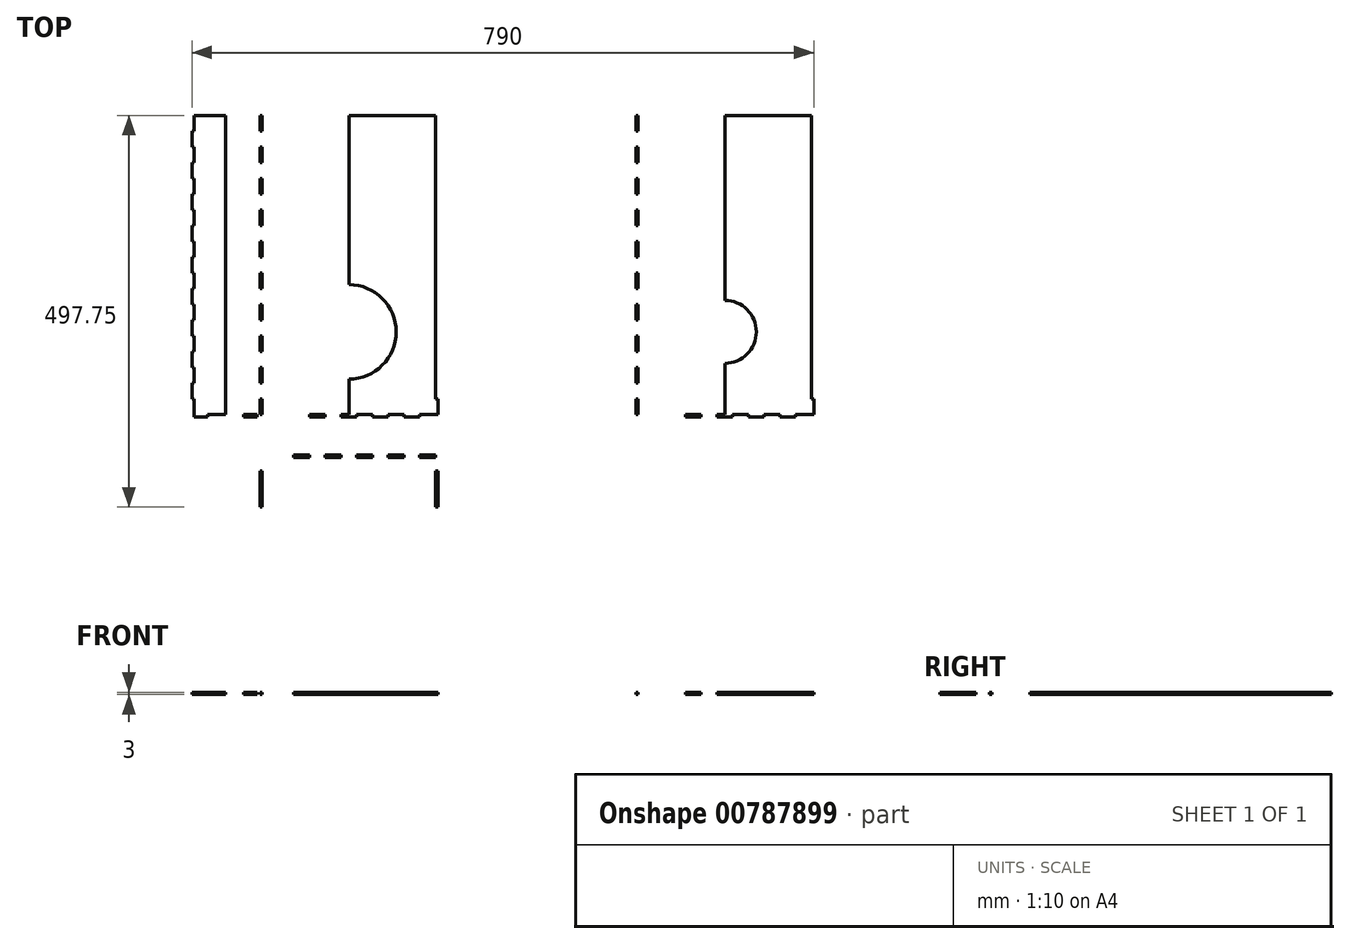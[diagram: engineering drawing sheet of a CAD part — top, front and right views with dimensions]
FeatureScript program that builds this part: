
annotation { "Feature Type Name" : "Feature", "Feature Type Description" : "" }
export const myFeature = defineFeature(function(context is Context, id is Id, definition is map)
    precondition{}
    {
        {
            var Q0;
            Q0=qCreatedBy(makeId("Top.planeOp"),FACE);
            var sketch = newSketch(context, id + "F0", { "sketchPlane" : qUnion([Q0])});
            skCircle(sketch, "E0", {"center": v(0, 0) * mm, "radius": 60 * mm});
            skLineSegment(sketch, "E1.bottom", {"start": v(0, -105) * mm, "end": v(110, -105) * mm});
            skLineSegment(sketch, "E1.top", {"start": v(0, 275) * mm, "end": v(110, 275) * mm});
            skLineSegment(sketch, "E1.left", {"start": v(0, -105) * mm, "end": v(0, 275) * mm});
            skLineSegment(sketch, "E1.right", {"start": v(110, -105) * mm, "end": v(110, 275) * mm});
            skLineSegment(sketch, "E2.bottom", {"start": v(110, -105) * mm, "end": v(113, -105) * mm});
            skLineSegment(sketch, "E2.top", {"start": v(110, -85) * mm, "end": v(113, -85) * mm});
            skLineSegment(sketch, "E2.left", {"start": v(110, -105) * mm, "end": v(110, -85) * mm});
            skLineSegment(sketch, "E2.right", {"start": v(113, -105) * mm, "end": v(113, -85) * mm});
            skLineSegment(sketch, "E3.0.1.0", {"start": v(110, -65) * mm, "end": v(110, -45) * mm});
            skLineSegment(sketch, "E3.0.1.1", {"start": v(113, -65) * mm, "end": v(113, -45) * mm});
            skLineSegment(sketch, "E3.0.1.2", {"start": v(110, -45) * mm, "end": v(113, -45) * mm});
            skLineSegment(sketch, "E3.0.1.3", {"start": v(110, -65) * mm, "end": v(113, -65) * mm});
            skLineSegment(sketch, "E3.0.2.0", {"start": v(110, -25) * mm, "end": v(110, -5) * mm});
            skLineSegment(sketch, "E3.0.2.1", {"start": v(113, -25) * mm, "end": v(113, -5) * mm});
            skLineSegment(sketch, "E3.0.2.2", {"start": v(110, -5) * mm, "end": v(113, -5) * mm});
            skLineSegment(sketch, "E3.0.2.3", {"start": v(110, -25) * mm, "end": v(113, -25) * mm});
            skLineSegment(sketch, "E3.0.3.0", {"start": v(110, 15) * mm, "end": v(110, 35) * mm});
            skLineSegment(sketch, "E3.0.3.1", {"start": v(113, 15) * mm, "end": v(113, 35) * mm});
            skLineSegment(sketch, "E3.0.3.2", {"start": v(110, 35) * mm, "end": v(113, 35) * mm});
            skLineSegment(sketch, "E3.0.3.3", {"start": v(110, 15) * mm, "end": v(113, 15) * mm});
            skLineSegment(sketch, "E3.0.4.0", {"start": v(110, 55) * mm, "end": v(110, 75) * mm});
            skLineSegment(sketch, "E3.0.4.1", {"start": v(113, 55) * mm, "end": v(113, 75) * mm});
            skLineSegment(sketch, "E3.0.4.2", {"start": v(110, 75) * mm, "end": v(113, 75) * mm});
            skLineSegment(sketch, "E3.0.4.3", {"start": v(110, 55) * mm, "end": v(113, 55) * mm});
            skLineSegment(sketch, "E3.0.5.0", {"start": v(110, 95) * mm, "end": v(110, 115) * mm});
            skLineSegment(sketch, "E3.0.5.1", {"start": v(113, 95) * mm, "end": v(113, 115) * mm});
            skLineSegment(sketch, "E3.0.5.2", {"start": v(110, 115) * mm, "end": v(113, 115) * mm});
            skLineSegment(sketch, "E3.0.5.3", {"start": v(110, 95) * mm, "end": v(113, 95) * mm});
            skLineSegment(sketch, "E3.0.6.0", {"start": v(110, 135) * mm, "end": v(110, 155) * mm});
            skLineSegment(sketch, "E3.0.6.1", {"start": v(113, 135) * mm, "end": v(113, 155) * mm});
            skLineSegment(sketch, "E3.0.6.2", {"start": v(110, 155) * mm, "end": v(113, 155) * mm});
            skLineSegment(sketch, "E3.0.6.3", {"start": v(110, 135) * mm, "end": v(113, 135) * mm});
            skLineSegment(sketch, "E3.0.7.0", {"start": v(110, 175) * mm, "end": v(110, 195) * mm});
            skLineSegment(sketch, "E3.0.7.1", {"start": v(113, 175) * mm, "end": v(113, 195) * mm});
            skLineSegment(sketch, "E3.0.7.2", {"start": v(110, 195) * mm, "end": v(113, 195) * mm});
            skLineSegment(sketch, "E3.0.7.3", {"start": v(110, 175) * mm, "end": v(113, 175) * mm});
            skLineSegment(sketch, "E3.0.8.0", {"start": v(110, 215) * mm, "end": v(110, 235) * mm});
            skLineSegment(sketch, "E3.0.8.1", {"start": v(113, 215) * mm, "end": v(113, 235) * mm});
            skLineSegment(sketch, "E3.0.8.2", {"start": v(110, 235) * mm, "end": v(113, 235) * mm});
            skLineSegment(sketch, "E3.0.8.3", {"start": v(110, 215) * mm, "end": v(113, 215) * mm});
            skLineSegment(sketch, "E3.0.9.0", {"start": v(110, 255) * mm, "end": v(110, 275) * mm});
            skLineSegment(sketch, "E3.0.9.1", {"start": v(113, 255) * mm, "end": v(113, 275) * mm});
            skLineSegment(sketch, "E3.0.9.2", {"start": v(110, 275) * mm, "end": v(113, 275) * mm});
            skLineSegment(sketch, "E3.0.9.3", {"start": v(110, 255) * mm, "end": v(113, 255) * mm});
            skLineSegment(sketch, "E3.direction1", {"start": v(110, -105) * mm, "end": v(125, -105) * mm, "construction": true});
            skLineSegment(sketch, "E3.direction2", {"start": v(110, -105) * mm, "end": v(110, -65) * mm, "construction": true});
            skLineSegment(sketch, "E4.MirrorCS", {"start": v(-110, -105) * mm, "end": v(-113, -105) * mm});
            skLineSegment(sketch, "E5.MirrorCS", {"start": v(-110, 255) * mm, "end": v(-113, 255) * mm});
            skLineSegment(sketch, "E6.MirrorCS", {"start": v(-110, -85) * mm, "end": v(-113, -85) * mm});
            skLineSegment(sketch, "E7.MirrorCS", {"start": v(-110, 275) * mm, "end": v(-113, 275) * mm});
            skLineSegment(sketch, "E8.MirrorCS", {"start": v(-110, -5) * mm, "end": v(-113, -5) * mm});
            skLineSegment(sketch, "E9.MirrorCS", {"start": v(-110, 195) * mm, "end": v(-113, 195) * mm});
            skLineSegment(sketch, "E10.MirrorCS", {"start": v(-110, 155) * mm, "end": v(-113, 155) * mm});
            skLineSegment(sketch, "E11.MirrorCS", {"start": v(-110, 35) * mm, "end": v(-113, 35) * mm});
            skLineSegment(sketch, "E12.MirrorCS", {"start": v(-110, -45) * mm, "end": v(-113, -45) * mm});
            skLineSegment(sketch, "E13.MirrorCS", {"start": v(-110, -25) * mm, "end": v(-113, -25) * mm});
            skLineSegment(sketch, "E14.MirrorCS", {"start": v(-110, 135) * mm, "end": v(-113, 135) * mm});
            skLineSegment(sketch, "E15.MirrorCS", {"start": v(-110, -65) * mm, "end": v(-113, -65) * mm});
            skLineSegment(sketch, "E16.MirrorCS", {"start": v(-110, 175) * mm, "end": v(-113, 175) * mm});
            skLineSegment(sketch, "E17.MirrorCS", {"start": v(-110, 115) * mm, "end": v(-113, 115) * mm});
            skLineSegment(sketch, "E18.MirrorCS", {"start": v(-110, 75) * mm, "end": v(-113, 75) * mm});
            skLineSegment(sketch, "E19.MirrorCS", {"start": v(-110, 15) * mm, "end": v(-113, 15) * mm});
            skLineSegment(sketch, "E20.MirrorCS", {"start": v(-110, 95) * mm, "end": v(-113, 95) * mm});
            skLineSegment(sketch, "E21.MirrorCS", {"start": v(-110, 235) * mm, "end": v(-113, 235) * mm});
            skLineSegment(sketch, "E22.MirrorCS", {"start": v(-110, 215) * mm, "end": v(-113, 215) * mm});
            skLineSegment(sketch, "E23.MirrorCS", {"start": v(-110, 55) * mm, "end": v(-113, 55) * mm});
            skLineSegment(sketch, "E24.MirrorCS", {"start": v(-110, 135) * mm, "end": v(-110, 155) * mm});
            skLineSegment(sketch, "E25.MirrorCS", {"start": v(-113, -105) * mm, "end": v(-113, -85) * mm});
            skLineSegment(sketch, "E26.MirrorCS", {"start": v(-110, -65) * mm, "end": v(-110, -45) * mm});
            skLineSegment(sketch, "E27.MirrorCS", {"start": v(-110, -105) * mm, "end": v(-110, -65) * mm, "construction": true});
            skLineSegment(sketch, "E28.MirrorCS", {"start": v(-113, -65) * mm, "end": v(-113, -45) * mm});
            skLineSegment(sketch, "E29.MirrorCS", {"start": v(-113, 255) * mm, "end": v(-113, 275) * mm});
            skLineSegment(sketch, "E30.MirrorCS", {"start": v(-113, 95) * mm, "end": v(-113, 115) * mm});
            skLineSegment(sketch, "E31.MirrorCS", {"start": v(-110, -105) * mm, "end": v(-110, 275) * mm});
            skLineSegment(sketch, "E32.MirrorCS", {"start": v(-113, -25) * mm, "end": v(-113, -5) * mm});
            skLineSegment(sketch, "E33.MirrorCS", {"start": v(-113, 55) * mm, "end": v(-113, 75) * mm});
            skLineSegment(sketch, "E34.MirrorCS", {"start": v(-113, 135) * mm, "end": v(-113, 155) * mm});
            skLineSegment(sketch, "E35.MirrorCS", {"start": v(-110, 215) * mm, "end": v(-110, 235) * mm});
            skLineSegment(sketch, "E36.MirrorCS", {"start": v(-110, 255) * mm, "end": v(-110, 275) * mm});
            skLineSegment(sketch, "E37.MirrorCS", {"start": v(-110, 175) * mm, "end": v(-110, 195) * mm});
            skLineSegment(sketch, "E38.MirrorCS", {"start": v(-113, 215) * mm, "end": v(-113, 235) * mm});
            skLineSegment(sketch, "E39.MirrorCS", {"start": v(-110, -25) * mm, "end": v(-110, -5) * mm});
            skLineSegment(sketch, "E40.MirrorCS", {"start": v(-110, -105) * mm, "end": v(-110, -85) * mm});
            skLineSegment(sketch, "E41.MirrorCS", {"start": v(-110, 55) * mm, "end": v(-110, 75) * mm});
            skLineSegment(sketch, "E42.MirrorCS", {"start": v(-110, 15) * mm, "end": v(-110, 35) * mm});
            skLineSegment(sketch, "E43.MirrorCS", {"start": v(-110, 95) * mm, "end": v(-110, 115) * mm});
            skLineSegment(sketch, "E44.MirrorCS", {"start": v(-113, 15) * mm, "end": v(-113, 35) * mm});
            skLineSegment(sketch, "E45.MirrorCS", {"start": v(-113, 175) * mm, "end": v(-113, 195) * mm});
            skLineSegment(sketch, "E46.MirrorCS", {"start": v(-110, -105) * mm, "end": v(-125, -105) * mm, "construction": true});
            skLineSegment(sketch, "E47.MirrorCS", {"start": v(0, 275) * mm, "end": v(-110, 275) * mm});
            skLineSegment(sketch, "E48.MirrorCS", {"start": v(0, -105) * mm, "end": v(-110, -105) * mm});
            skLineSegment(sketch, "E49.bottom", {"start": v(-156.5, -125) * mm, "end": v(-116.5, -125) * mm});
            skLineSegment(sketch, "E49.top", {"start": v(-156.5, 455) * mm, "end": v(-116.5, 455) * mm});
            skLineSegment(sketch, "E49.left", {"start": v(-156.5, -125) * mm, "end": v(-156.5, 455) * mm});
            skLineSegment(sketch, "E49.right", {"start": v(-116.5, -125) * mm, "end": v(-116.5, 455) * mm});
            skLineSegment(sketch, "E50.bottom", {"start": v(-116.5, -125) * mm, "end": v(-113.5, -125) * mm});
            skLineSegment(sketch, "E50.top", {"start": v(-116.5, -105) * mm, "end": v(-113.5, -105) * mm});
            skLineSegment(sketch, "E50.left", {"start": v(-116.5, -125) * mm, "end": v(-116.5, -105) * mm});
            skLineSegment(sketch, "E50.right", {"start": v(-113.5, -125) * mm, "end": v(-113.5, -105) * mm});
            skLineSegment(sketch, "E51.0.1.0", {"start": v(-116.5, -85) * mm, "end": v(-116.5, -65) * mm});
            skLineSegment(sketch, "E51.0.1.1", {"start": v(-113.5, -85) * mm, "end": v(-113.5, -65) * mm});
            skLineSegment(sketch, "E51.0.1.2", {"start": v(-116.5, -65) * mm, "end": v(-113.5, -65) * mm});
            skLineSegment(sketch, "E51.0.1.3", {"start": v(-116.5, -85) * mm, "end": v(-113.5, -85) * mm});
            skLineSegment(sketch, "E51.0.2.0", {"start": v(-116.5, -45) * mm, "end": v(-116.5, -25) * mm});
            skLineSegment(sketch, "E51.0.2.1", {"start": v(-113.5, -45) * mm, "end": v(-113.5, -25) * mm});
            skLineSegment(sketch, "E51.0.2.2", {"start": v(-116.5, -25) * mm, "end": v(-113.5, -25) * mm});
            skLineSegment(sketch, "E51.0.2.3", {"start": v(-116.5, -45) * mm, "end": v(-113.5, -45) * mm});
            skLineSegment(sketch, "E51.0.3.0", {"start": v(-116.5, -5) * mm, "end": v(-116.5, 15) * mm});
            skLineSegment(sketch, "E51.0.3.1", {"start": v(-113.5, -5) * mm, "end": v(-113.5, 15) * mm});
            skLineSegment(sketch, "E51.0.3.2", {"start": v(-116.5, 15) * mm, "end": v(-113.5, 15) * mm});
            skLineSegment(sketch, "E51.0.3.3", {"start": v(-116.5, -5) * mm, "end": v(-113.5, -5) * mm});
            skLineSegment(sketch, "E51.0.4.0", {"start": v(-116.5, 35) * mm, "end": v(-116.5, 55) * mm});
            skLineSegment(sketch, "E51.0.4.1", {"start": v(-113.5, 35) * mm, "end": v(-113.5, 55) * mm});
            skLineSegment(sketch, "E51.0.4.2", {"start": v(-116.5, 55) * mm, "end": v(-113.5, 55) * mm});
            skLineSegment(sketch, "E51.0.4.3", {"start": v(-116.5, 35) * mm, "end": v(-113.5, 35) * mm});
            skLineSegment(sketch, "E51.0.5.0", {"start": v(-116.5, 75) * mm, "end": v(-116.5, 95) * mm});
            skLineSegment(sketch, "E51.0.5.1", {"start": v(-113.5, 75) * mm, "end": v(-113.5, 95) * mm});
            skLineSegment(sketch, "E51.0.5.2", {"start": v(-116.5, 95) * mm, "end": v(-113.5, 95) * mm});
            skLineSegment(sketch, "E51.0.5.3", {"start": v(-116.5, 75) * mm, "end": v(-113.5, 75) * mm});
            skLineSegment(sketch, "E51.0.6.0", {"start": v(-116.5, 115) * mm, "end": v(-116.5, 135) * mm});
            skLineSegment(sketch, "E51.0.6.1", {"start": v(-113.5, 115) * mm, "end": v(-113.5, 135) * mm});
            skLineSegment(sketch, "E51.0.6.2", {"start": v(-116.5, 135) * mm, "end": v(-113.5, 135) * mm});
            skLineSegment(sketch, "E51.0.6.3", {"start": v(-116.5, 115) * mm, "end": v(-113.5, 115) * mm});
            skLineSegment(sketch, "E51.0.7.0", {"start": v(-116.5, 155) * mm, "end": v(-116.5, 175) * mm});
            skLineSegment(sketch, "E51.0.7.1", {"start": v(-113.5, 155) * mm, "end": v(-113.5, 175) * mm});
            skLineSegment(sketch, "E51.0.7.2", {"start": v(-116.5, 175) * mm, "end": v(-113.5, 175) * mm});
            skLineSegment(sketch, "E51.0.7.3", {"start": v(-116.5, 155) * mm, "end": v(-113.5, 155) * mm});
            skLineSegment(sketch, "E51.0.8.0", {"start": v(-116.5, 195) * mm, "end": v(-116.5, 215) * mm});
            skLineSegment(sketch, "E51.0.8.1", {"start": v(-113.5, 195) * mm, "end": v(-113.5, 215) * mm});
            skLineSegment(sketch, "E51.0.8.2", {"start": v(-116.5, 215) * mm, "end": v(-113.5, 215) * mm});
            skLineSegment(sketch, "E51.0.8.3", {"start": v(-116.5, 195) * mm, "end": v(-113.5, 195) * mm});
            skLineSegment(sketch, "E51.0.9.0", {"start": v(-116.5, 235) * mm, "end": v(-116.5, 255) * mm});
            skLineSegment(sketch, "E51.0.9.1", {"start": v(-113.5, 235) * mm, "end": v(-113.5, 255) * mm});
            skLineSegment(sketch, "E51.0.9.2", {"start": v(-116.5, 255) * mm, "end": v(-113.5, 255) * mm});
            skLineSegment(sketch, "E51.0.9.3", {"start": v(-116.5, 235) * mm, "end": v(-113.5, 235) * mm});
            skLineSegment(sketch, "E51.direction1", {"start": v(-273.42, -125) * mm, "end": v(-116.5, -125) * mm, "construction": true});
            skLineSegment(sketch, "E51.direction2", {"start": v(-116.5, -125) * mm, "end": v(-116.5, -85) * mm, "construction": true});
            skLineSegment(sketch, "E52", {"start": v(-116.5, 435) * mm, "end": v(-156.5, 435) * mm});
            skLineSegment(sketch, "E53", {"start": v(-116.5, -105) * mm, "end": v(-156.5, -105) * mm});
            skLineSegment(sketch, "E54.MirrorCS", {"start": v(-196.5, -125) * mm, "end": v(-199.5, -125) * mm});
            skLineSegment(sketch, "E55.MirrorCS", {"start": v(-196.5, -105) * mm, "end": v(-199.5, -105) * mm});
            skLineSegment(sketch, "E56.MirrorCS", {"start": v(-199.5, -125) * mm, "end": v(-199.5, -105) * mm});
            skLineSegment(sketch, "E57.MirrorCS", {"start": v(-196.5, -125) * mm, "end": v(-196.5, -85) * mm, "construction": true});
            skLineSegment(sketch, "E58.MirrorCS", {"start": v(-196.5, -85) * mm, "end": v(-199.5, -85) * mm});
            skLineSegment(sketch, "E59.MirrorCS", {"start": v(-196.5, -125) * mm, "end": v(-196.5, -105) * mm});
            skLineSegment(sketch, "E60.MirrorCS", {"start": v(-196.5, -85) * mm, "end": v(-196.5, -65) * mm});
            skLineSegment(sketch, "E61.MirrorCS", {"start": v(-196.5, 35) * mm, "end": v(-199.5, 35) * mm});
            skLineSegment(sketch, "E62.MirrorCS", {"start": v(-196.5, 195) * mm, "end": v(-199.5, 195) * mm});
            skLineSegment(sketch, "E63.MirrorCS", {"start": v(-199.5, 35) * mm, "end": v(-199.5, 55) * mm});
            skLineSegment(sketch, "E64.MirrorCS", {"start": v(-199.5, -85) * mm, "end": v(-199.5, -65) * mm});
            skLineSegment(sketch, "E65.MirrorCS", {"start": v(-199.5, -45) * mm, "end": v(-199.5, -25) * mm});
            skLineSegment(sketch, "E66.MirrorCS", {"start": v(-196.5, -45) * mm, "end": v(-196.5, -25) * mm});
            skLineSegment(sketch, "E67.MirrorCS", {"start": v(-196.5, 115) * mm, "end": v(-196.5, 135) * mm});
            skLineSegment(sketch, "E68.MirrorCS", {"start": v(-196.5, -25) * mm, "end": v(-199.5, -25) * mm});
            skLineSegment(sketch, "E69.MirrorCS", {"start": v(-196.5, 15) * mm, "end": v(-199.5, 15) * mm});
            skLineSegment(sketch, "E70.MirrorCS", {"start": v(-196.5, 215) * mm, "end": v(-199.5, 215) * mm});
            skLineSegment(sketch, "E71.MirrorCS", {"start": v(-196.5, -5) * mm, "end": v(-196.5, 15) * mm});
            skLineSegment(sketch, "E72.MirrorCS", {"start": v(-196.5, 195) * mm, "end": v(-196.5, 215) * mm});
            skLineSegment(sketch, "E73.MirrorCS", {"start": v(-199.5, 195) * mm, "end": v(-199.5, 215) * mm});
            skLineSegment(sketch, "E74.MirrorCS", {"start": v(-199.5, 115) * mm, "end": v(-199.5, 135) * mm});
            skLineSegment(sketch, "E75.MirrorCS", {"start": v(-196.5, 135) * mm, "end": v(-199.5, 135) * mm});
            skLineSegment(sketch, "E76.MirrorCS", {"start": v(-199.5, -5) * mm, "end": v(-199.5, 15) * mm});
            skLineSegment(sketch, "E77.MirrorCS", {"start": v(-196.5, 175) * mm, "end": v(-199.5, 175) * mm});
            skLineSegment(sketch, "E78.MirrorCS", {"start": v(-196.5, 75) * mm, "end": v(-199.5, 75) * mm});
            skLineSegment(sketch, "E79.MirrorCS", {"start": v(-196.5, 235) * mm, "end": v(-199.5, 235) * mm});
            skLineSegment(sketch, "E80.MirrorCS", {"start": v(-196.5, 55) * mm, "end": v(-199.5, 55) * mm});
            skLineSegment(sketch, "E81.MirrorCS", {"start": v(-196.5, 35) * mm, "end": v(-196.5, 55) * mm});
            skLineSegment(sketch, "E82.MirrorCS", {"start": v(-196.5, -45) * mm, "end": v(-199.5, -45) * mm});
            skLineSegment(sketch, "E83.MirrorCS", {"start": v(-196.5, -65) * mm, "end": v(-199.5, -65) * mm});
            skLineSegment(sketch, "E84.MirrorCS", {"start": v(-196.5, 255) * mm, "end": v(-199.5, 255) * mm});
            skLineSegment(sketch, "E85.MirrorCS", {"start": v(-196.5, 95) * mm, "end": v(-199.5, 95) * mm});
            skLineSegment(sketch, "E86.MirrorCS", {"start": v(-196.5, -5) * mm, "end": v(-199.5, -5) * mm});
            skLineSegment(sketch, "E87.MirrorCS", {"start": v(-196.5, 115) * mm, "end": v(-199.5, 115) * mm});
            skLineSegment(sketch, "E88.MirrorCS", {"start": v(-196.5, 155) * mm, "end": v(-199.5, 155) * mm});
            skLineSegment(sketch, "E89.MirrorCS", {"start": v(-156.5, -125) * mm, "end": v(-196.5, -125) * mm});
            skLineSegment(sketch, "E90.MirrorCS", {"start": v(-196.5, 155) * mm, "end": v(-196.5, 175) * mm});
            skLineSegment(sketch, "E91.MirrorCS", {"start": v(-196.5, 75) * mm, "end": v(-196.5, 95) * mm});
            skLineSegment(sketch, "E92.MirrorCS", {"start": v(-196.5, 235) * mm, "end": v(-196.5, 255) * mm});
            skLineSegment(sketch, "E93.MirrorCS", {"start": v(-199.5, 75) * mm, "end": v(-199.5, 95) * mm});
            skLineSegment(sketch, "E94.MirrorCS", {"start": v(-156.5, 455) * mm, "end": v(-196.5, 455) * mm});
            skLineSegment(sketch, "E95.MirrorCS", {"start": v(-199.5, 235) * mm, "end": v(-199.5, 255) * mm});
            skLineSegment(sketch, "E96.MirrorCS", {"start": v(-199.5, 155) * mm, "end": v(-199.5, 175) * mm});
            skLineSegment(sketch, "E97.MirrorCS", {"start": v(-196.5, -105) * mm, "end": v(-156.5, -105) * mm});
            skLineSegment(sketch, "E98.MirrorCS", {"start": v(-196.5, -125) * mm, "end": v(-196.5, 455) * mm});
            skLineSegment(sketch, "E99.MirrorCS", {"start": v(-196.5, 435) * mm, "end": v(-156.5, 435) * mm});
            skLineSegment(sketch, "E100.bottom", {"start": v(-90, -105) * mm, "end": v(-70, -105) * mm});
            skLineSegment(sketch, "E100.top", {"start": v(-90, -108) * mm, "end": v(-70, -108) * mm});
            skLineSegment(sketch, "E100.left", {"start": v(-90, -105) * mm, "end": v(-90, -108) * mm});
            skLineSegment(sketch, "E100.right", {"start": v(-70, -105) * mm, "end": v(-70, -108) * mm});
            skLineSegment(sketch, "E101.1.0.0", {"start": v(-50, -108) * mm, "end": v(-30, -108) * mm});
            skLineSegment(sketch, "E101.1.0.1", {"start": v(-50, -105) * mm, "end": v(-30, -105) * mm});
            skLineSegment(sketch, "E101.1.0.2", {"start": v(-50, -105) * mm, "end": v(-50, -108) * mm});
            skLineSegment(sketch, "E101.1.0.3", {"start": v(-30, -105) * mm, "end": v(-30, -108) * mm});
            skLineSegment(sketch, "E101.2.0.0", {"start": v(-10, -108) * mm, "end": v(10, -108) * mm});
            skLineSegment(sketch, "E101.2.0.1", {"start": v(-10, -105) * mm, "end": v(10, -105) * mm});
            skLineSegment(sketch, "E101.2.0.2", {"start": v(-10, -105) * mm, "end": v(-10, -108) * mm});
            skLineSegment(sketch, "E101.2.0.3", {"start": v(10, -105) * mm, "end": v(10, -108) * mm});
            skLineSegment(sketch, "E101.3.0.0", {"start": v(30, -108) * mm, "end": v(50, -108) * mm});
            skLineSegment(sketch, "E101.3.0.1", {"start": v(30, -105) * mm, "end": v(50, -105) * mm});
            skLineSegment(sketch, "E101.3.0.2", {"start": v(30, -105) * mm, "end": v(30, -108) * mm});
            skLineSegment(sketch, "E101.3.0.3", {"start": v(50, -105) * mm, "end": v(50, -108) * mm});
            skLineSegment(sketch, "E101.direction1", {"start": v(-90, -108) * mm, "end": v(-50, -108) * mm, "construction": true});
            skLineSegment(sketch, "E102.0.4.0", {"start": v(70, -108) * mm, "end": v(90, -108) * mm});
            skLineSegment(sketch, "E102.3.4.0", {"start": v(70, -105) * mm, "end": v(90, -105) * mm});
            skLineSegment(sketch, "E102.6.4.0", {"start": v(70, -105) * mm, "end": v(70, -108) * mm});
            skLineSegment(sketch, "E102.9.4.0", {"start": v(90, -105) * mm, "end": v(90, -108) * mm});
            skLineSegment(sketch, "E103.bottom", {"start": v(-199.5, -105) * mm, "end": v(-179.5, -105) * mm});
            skLineSegment(sketch, "E103.top", {"start": v(-199.5, -108) * mm, "end": v(-179.5, -108) * mm});
            skLineSegment(sketch, "E103.left", {"start": v(-199.5, -105) * mm, "end": v(-199.5, -108) * mm});
            skLineSegment(sketch, "E103.right", {"start": v(-179.5, -105) * mm, "end": v(-179.5, -108) * mm});
            skLineSegment(sketch, "E104.bottom", {"start": v(-113.5, -105) * mm, "end": v(-133.5, -105) * mm});
            skLineSegment(sketch, "E104.top", {"start": v(-113.5, -108) * mm, "end": v(-133.5, -108) * mm});
            skLineSegment(sketch, "E104.left", {"start": v(-113.5, -105) * mm, "end": v(-113.5, -108) * mm});
            skLineSegment(sketch, "E104.right", {"start": v(-133.5, -105) * mm, "end": v(-133.5, -108) * mm});
            skLineSegment(sketch, "E105.bottom", {"start": v(-110, -159.75) * mm, "end": v(110, -159.75) * mm});
            skLineSegment(sketch, "E105.top", {"start": v(-110, -239.75) * mm, "end": v(110, -239.75) * mm});
            skLineSegment(sketch, "E105.left", {"start": v(-110, -159.75) * mm, "end": v(-110, -239.75) * mm});
            skLineSegment(sketch, "E105.right", {"start": v(110, -159.75) * mm, "end": v(110, -239.75) * mm});
            skLineSegment(sketch, "E106.bottom", {"start": v(-110, -159.75) * mm, "end": v(-90, -159.75) * mm});
            skLineSegment(sketch, "E106.top", {"start": v(-110, -156.75) * mm, "end": v(-90, -156.75) * mm});
            skLineSegment(sketch, "E106.left", {"start": v(-110, -159.75) * mm, "end": v(-110, -156.75) * mm});
            skLineSegment(sketch, "E106.right", {"start": v(-90, -159.75) * mm, "end": v(-90, -156.75) * mm});
            skLineSegment(sketch, "E107.0.1.0", {"start": v(-110, -239.75) * mm, "end": v(-90, -239.75) * mm});
            skLineSegment(sketch, "E107.0.1.1", {"start": v(-110, -242.75) * mm, "end": v(-110, -239.75) * mm});
            skLineSegment(sketch, "E107.0.1.2", {"start": v(-90, -242.75) * mm, "end": v(-90, -239.75) * mm});
            skLineSegment(sketch, "E107.0.1.3", {"start": v(-110, -242.75) * mm, "end": v(-90, -242.75) * mm});
            skLineSegment(sketch, "E107.1.0.0", {"start": v(-70, -156.75) * mm, "end": v(-50, -156.75) * mm});
            skLineSegment(sketch, "E107.1.0.1", {"start": v(-70, -159.75) * mm, "end": v(-70, -156.75) * mm});
            skLineSegment(sketch, "E107.1.0.2", {"start": v(-50, -159.75) * mm, "end": v(-50, -156.75) * mm});
            skLineSegment(sketch, "E107.1.0.3", {"start": v(-70, -159.75) * mm, "end": v(-50, -159.75) * mm});
            skLineSegment(sketch, "E107.1.1.0", {"start": v(-70, -239.75) * mm, "end": v(-50, -239.75) * mm});
            skLineSegment(sketch, "E107.1.1.1", {"start": v(-70, -242.75) * mm, "end": v(-70, -239.75) * mm});
            skLineSegment(sketch, "E107.1.1.2", {"start": v(-50, -242.75) * mm, "end": v(-50, -239.75) * mm});
            skLineSegment(sketch, "E107.1.1.3", {"start": v(-70, -242.75) * mm, "end": v(-50, -242.75) * mm});
            skLineSegment(sketch, "E107.2.0.0", {"start": v(-30, -156.75) * mm, "end": v(-10, -156.75) * mm});
            skLineSegment(sketch, "E107.2.0.1", {"start": v(-30, -159.75) * mm, "end": v(-30, -156.75) * mm});
            skLineSegment(sketch, "E107.2.0.2", {"start": v(-10, -159.75) * mm, "end": v(-10, -156.75) * mm});
            skLineSegment(sketch, "E107.2.0.3", {"start": v(-30, -159.75) * mm, "end": v(-10, -159.75) * mm});
            skLineSegment(sketch, "E107.2.1.0", {"start": v(-30, -239.75) * mm, "end": v(-10, -239.75) * mm});
            skLineSegment(sketch, "E107.2.1.1", {"start": v(-30, -242.75) * mm, "end": v(-30, -239.75) * mm});
            skLineSegment(sketch, "E107.2.1.2", {"start": v(-10, -242.75) * mm, "end": v(-10, -239.75) * mm});
            skLineSegment(sketch, "E107.2.1.3", {"start": v(-30, -242.75) * mm, "end": v(-10, -242.75) * mm});
            skLineSegment(sketch, "E107.3.0.0", {"start": v(10, -156.75) * mm, "end": v(30, -156.75) * mm});
            skLineSegment(sketch, "E107.3.0.1", {"start": v(10, -159.75) * mm, "end": v(10, -156.75) * mm});
            skLineSegment(sketch, "E107.3.0.2", {"start": v(30, -159.75) * mm, "end": v(30, -156.75) * mm});
            skLineSegment(sketch, "E107.3.0.3", {"start": v(10, -159.75) * mm, "end": v(30, -159.75) * mm});
            skLineSegment(sketch, "E107.3.1.0", {"start": v(10, -239.75) * mm, "end": v(30, -239.75) * mm});
            skLineSegment(sketch, "E107.3.1.1", {"start": v(10, -242.75) * mm, "end": v(10, -239.75) * mm});
            skLineSegment(sketch, "E107.3.1.2", {"start": v(30, -242.75) * mm, "end": v(30, -239.75) * mm});
            skLineSegment(sketch, "E107.3.1.3", {"start": v(10, -242.75) * mm, "end": v(30, -242.75) * mm});
            skLineSegment(sketch, "E107.4.0.0", {"start": v(50, -156.75) * mm, "end": v(70, -156.75) * mm});
            skLineSegment(sketch, "E107.4.0.1", {"start": v(50, -159.75) * mm, "end": v(50, -156.75) * mm});
            skLineSegment(sketch, "E107.4.0.2", {"start": v(70, -159.75) * mm, "end": v(70, -156.75) * mm});
            skLineSegment(sketch, "E107.4.0.3", {"start": v(50, -159.75) * mm, "end": v(70, -159.75) * mm});
            skLineSegment(sketch, "E107.4.1.0", {"start": v(50, -239.75) * mm, "end": v(70, -239.75) * mm});
            skLineSegment(sketch, "E107.4.1.1", {"start": v(50, -242.75) * mm, "end": v(50, -239.75) * mm});
            skLineSegment(sketch, "E107.4.1.2", {"start": v(70, -242.75) * mm, "end": v(70, -239.75) * mm});
            skLineSegment(sketch, "E107.4.1.3", {"start": v(50, -242.75) * mm, "end": v(70, -242.75) * mm});
            skLineSegment(sketch, "E107.5.0.0", {"start": v(90, -156.75) * mm, "end": v(110, -156.75) * mm});
            skLineSegment(sketch, "E107.5.0.1", {"start": v(90, -159.75) * mm, "end": v(90, -156.75) * mm});
            skLineSegment(sketch, "E107.5.0.2", {"start": v(110, -159.75) * mm, "end": v(110, -156.75) * mm});
            skLineSegment(sketch, "E107.5.0.3", {"start": v(90, -159.75) * mm, "end": v(110, -159.75) * mm});
            skLineSegment(sketch, "E107.5.1.0", {"start": v(90, -239.75) * mm, "end": v(110, -239.75) * mm});
            skLineSegment(sketch, "E107.5.1.1", {"start": v(90, -242.75) * mm, "end": v(90, -239.75) * mm});
            skLineSegment(sketch, "E107.5.1.2", {"start": v(110, -242.75) * mm, "end": v(110, -239.75) * mm});
            skLineSegment(sketch, "E107.5.1.3", {"start": v(90, -242.75) * mm, "end": v(110, -242.75) * mm});
            skLineSegment(sketch, "E107.direction1", {"start": v(-110, -159.75) * mm, "end": v(-70, -159.75) * mm, "construction": true});
            skLineSegment(sketch, "E107.direction2", {"start": v(-110, -159.75) * mm, "end": v(-110, -242.75) * mm, "construction": true});
            skLineSegment(sketch, "E108.bottom", {"start": v(-110, -176.75) * mm, "end": v(-113, -176.75) * mm});
            skLineSegment(sketch, "E108.top", {"start": v(-110, -222.75) * mm, "end": v(-113, -222.75) * mm});
            skLineSegment(sketch, "E108.left", {"start": v(-110, -176.75) * mm, "end": v(-110, -222.75) * mm});
            skLineSegment(sketch, "E108.right", {"start": v(-113, -176.75) * mm, "end": v(-113, -222.75) * mm});
            skLineSegment(sketch, "E109.bottom", {"start": v(110, -176.75) * mm, "end": v(113, -176.75) * mm});
            skLineSegment(sketch, "E109.top", {"start": v(110, -222.75) * mm, "end": v(113, -222.75) * mm});
            skLineSegment(sketch, "E109.left", {"start": v(110, -176.75) * mm, "end": v(110, -222.75) * mm});
            skLineSegment(sketch, "E109.right", {"start": v(113, -176.75) * mm, "end": v(113, -222.75) * mm});
            skCircle(sketch, "E110", {"center": v(477.5, 0) * mm, "radius": 40 * mm});
            skLineSegment(sketch, "E111.bottom", {"start": v(477.5, -105) * mm, "end": v(587.5, -105) * mm});
            skLineSegment(sketch, "E111.top", {"start": v(477.5, 275) * mm, "end": v(587.5, 275) * mm});
            skLineSegment(sketch, "E111.left", {"start": v(477.5, -105) * mm, "end": v(477.5, 275) * mm});
            skLineSegment(sketch, "E111.right", {"start": v(587.5, -105) * mm, "end": v(587.5, 275) * mm});
            skLineSegment(sketch, "E112.bottom", {"start": v(587.5, -105) * mm, "end": v(590.5, -105) * mm});
            skLineSegment(sketch, "E112.top", {"start": v(587.5, -85) * mm, "end": v(590.5, -85) * mm});
            skLineSegment(sketch, "E112.left", {"start": v(587.5, -105) * mm, "end": v(587.5, -85) * mm});
            skLineSegment(sketch, "E112.right", {"start": v(590.5, -105) * mm, "end": v(590.5, -85) * mm});
            skLineSegment(sketch, "E113.0.1.0", {"start": v(587.5, -65) * mm, "end": v(587.5, -45) * mm});
            skLineSegment(sketch, "E113.0.1.1", {"start": v(590.5, -65) * mm, "end": v(590.5, -45) * mm});
            skLineSegment(sketch, "E113.0.1.2", {"start": v(587.5, -45) * mm, "end": v(590.5, -45) * mm});
            skLineSegment(sketch, "E113.0.1.3", {"start": v(587.5, -65) * mm, "end": v(590.5, -65) * mm});
            skLineSegment(sketch, "E113.0.2.0", {"start": v(587.5, -25) * mm, "end": v(587.5, -5) * mm});
            skLineSegment(sketch, "E113.0.2.1", {"start": v(590.5, -25) * mm, "end": v(590.5, -5) * mm});
            skLineSegment(sketch, "E113.0.2.2", {"start": v(587.5, -5) * mm, "end": v(590.5, -5) * mm});
            skLineSegment(sketch, "E113.0.2.3", {"start": v(587.5, -25) * mm, "end": v(590.5, -25) * mm});
            skLineSegment(sketch, "E113.0.3.0", {"start": v(587.5, 15) * mm, "end": v(587.5, 35) * mm});
            skLineSegment(sketch, "E113.0.3.1", {"start": v(590.5, 15) * mm, "end": v(590.5, 35) * mm});
            skLineSegment(sketch, "E113.0.3.2", {"start": v(587.5, 35) * mm, "end": v(590.5, 35) * mm});
            skLineSegment(sketch, "E113.0.3.3", {"start": v(587.5, 15) * mm, "end": v(590.5, 15) * mm});
            skLineSegment(sketch, "E113.0.4.0", {"start": v(587.5, 55) * mm, "end": v(587.5, 75) * mm});
            skLineSegment(sketch, "E113.0.4.1", {"start": v(590.5, 55) * mm, "end": v(590.5, 75) * mm});
            skLineSegment(sketch, "E113.0.4.2", {"start": v(587.5, 75) * mm, "end": v(590.5, 75) * mm});
            skLineSegment(sketch, "E113.0.4.3", {"start": v(587.5, 55) * mm, "end": v(590.5, 55) * mm});
            skLineSegment(sketch, "E113.0.5.0", {"start": v(587.5, 95) * mm, "end": v(587.5, 115) * mm});
            skLineSegment(sketch, "E113.0.5.1", {"start": v(590.5, 95) * mm, "end": v(590.5, 115) * mm});
            skLineSegment(sketch, "E113.0.5.2", {"start": v(587.5, 115) * mm, "end": v(590.5, 115) * mm});
            skLineSegment(sketch, "E113.0.5.3", {"start": v(587.5, 95) * mm, "end": v(590.5, 95) * mm});
            skLineSegment(sketch, "E113.0.6.0", {"start": v(587.5, 135) * mm, "end": v(587.5, 155) * mm});
            skLineSegment(sketch, "E113.0.6.1", {"start": v(590.5, 135) * mm, "end": v(590.5, 155) * mm});
            skLineSegment(sketch, "E113.0.6.2", {"start": v(587.5, 155) * mm, "end": v(590.5, 155) * mm});
            skLineSegment(sketch, "E113.0.6.3", {"start": v(587.5, 135) * mm, "end": v(590.5, 135) * mm});
            skLineSegment(sketch, "E113.0.7.0", {"start": v(587.5, 175) * mm, "end": v(587.5, 195) * mm});
            skLineSegment(sketch, "E113.0.7.1", {"start": v(590.5, 175) * mm, "end": v(590.5, 195) * mm});
            skLineSegment(sketch, "E113.0.7.2", {"start": v(587.5, 195) * mm, "end": v(590.5, 195) * mm});
            skLineSegment(sketch, "E113.0.7.3", {"start": v(587.5, 175) * mm, "end": v(590.5, 175) * mm});
            skLineSegment(sketch, "E113.0.8.0", {"start": v(587.5, 215) * mm, "end": v(587.5, 235) * mm});
            skLineSegment(sketch, "E113.0.8.1", {"start": v(590.5, 215) * mm, "end": v(590.5, 235) * mm});
            skLineSegment(sketch, "E113.0.8.2", {"start": v(587.5, 235) * mm, "end": v(590.5, 235) * mm});
            skLineSegment(sketch, "E113.0.8.3", {"start": v(587.5, 215) * mm, "end": v(590.5, 215) * mm});
            skLineSegment(sketch, "E113.0.9.0", {"start": v(587.5, 255) * mm, "end": v(587.5, 275) * mm});
            skLineSegment(sketch, "E113.0.9.1", {"start": v(590.5, 255) * mm, "end": v(590.5, 275) * mm});
            skLineSegment(sketch, "E113.0.9.2", {"start": v(587.5, 275) * mm, "end": v(590.5, 275) * mm});
            skLineSegment(sketch, "E113.0.9.3", {"start": v(587.5, 255) * mm, "end": v(590.5, 255) * mm});
            skLineSegment(sketch, "E113.direction1", {"start": v(509.1, -105) * mm, "end": v(587.5, -105) * mm, "construction": true});
            skLineSegment(sketch, "E113.direction2", {"start": v(587.5, -105) * mm, "end": v(587.5, -65) * mm, "construction": true});
            skLineSegment(sketch, "E114.MirrorCS", {"start": v(367.5, -105) * mm, "end": v(364.5, -105) * mm});
            skLineSegment(sketch, "E115.MirrorCS", {"start": v(367.5, 255) * mm, "end": v(364.5, 255) * mm});
            skLineSegment(sketch, "E116.MirrorCS", {"start": v(367.5, -85) * mm, "end": v(364.5, -85) * mm});
            skLineSegment(sketch, "E117.MirrorCS", {"start": v(367.5, 275) * mm, "end": v(364.5, 275) * mm});
            skLineSegment(sketch, "E118.MirrorCS", {"start": v(367.5, -5) * mm, "end": v(364.5, -5) * mm});
            skLineSegment(sketch, "E119.MirrorCS", {"start": v(367.5, 195) * mm, "end": v(364.5, 195) * mm});
            skLineSegment(sketch, "E120.MirrorCS", {"start": v(367.5, 155) * mm, "end": v(364.5, 155) * mm});
            skLineSegment(sketch, "E121.MirrorCS", {"start": v(367.5, 35) * mm, "end": v(364.5, 35) * mm});
            skLineSegment(sketch, "E122.MirrorCS", {"start": v(367.5, -45) * mm, "end": v(364.5, -45) * mm});
            skLineSegment(sketch, "E123.MirrorCS", {"start": v(367.5, -25) * mm, "end": v(364.5, -25) * mm});
            skLineSegment(sketch, "E124.MirrorCS", {"start": v(367.5, 135) * mm, "end": v(364.5, 135) * mm});
            skLineSegment(sketch, "E125.MirrorCS", {"start": v(367.5, -65) * mm, "end": v(364.5, -65) * mm});
            skLineSegment(sketch, "E126.MirrorCS", {"start": v(367.5, 175) * mm, "end": v(364.5, 175) * mm});
            skLineSegment(sketch, "E127.MirrorCS", {"start": v(367.5, 115) * mm, "end": v(364.5, 115) * mm});
            skLineSegment(sketch, "E128.MirrorCS", {"start": v(367.5, 75) * mm, "end": v(364.5, 75) * mm});
            skLineSegment(sketch, "E129.MirrorCS", {"start": v(367.5, 15) * mm, "end": v(364.5, 15) * mm});
            skLineSegment(sketch, "E130.MirrorCS", {"start": v(367.5, 95) * mm, "end": v(364.5, 95) * mm});
            skLineSegment(sketch, "E131.MirrorCS", {"start": v(367.5, 235) * mm, "end": v(364.5, 235) * mm});
            skLineSegment(sketch, "E132.MirrorCS", {"start": v(367.5, 215) * mm, "end": v(364.5, 215) * mm});
            skLineSegment(sketch, "E133.MirrorCS", {"start": v(367.5, 55) * mm, "end": v(364.5, 55) * mm});
            skLineSegment(sketch, "E134.MirrorCS", {"start": v(367.5, 135) * mm, "end": v(367.5, 155) * mm});
            skLineSegment(sketch, "E135.MirrorCS", {"start": v(364.5, -105) * mm, "end": v(364.5, -85) * mm});
            skLineSegment(sketch, "E136.MirrorCS", {"start": v(367.5, -65) * mm, "end": v(367.5, -45) * mm});
            skLineSegment(sketch, "E137.MirrorCS", {"start": v(367.5, -105) * mm, "end": v(367.5, -65) * mm, "construction": true});
            skLineSegment(sketch, "E138.MirrorCS", {"start": v(364.5, -65) * mm, "end": v(364.5, -45) * mm});
            skLineSegment(sketch, "E139.MirrorCS", {"start": v(364.5, 255) * mm, "end": v(364.5, 275) * mm});
            skLineSegment(sketch, "E140.MirrorCS", {"start": v(364.5, 95) * mm, "end": v(364.5, 115) * mm});
            skLineSegment(sketch, "E141.MirrorCS", {"start": v(367.5, -105) * mm, "end": v(367.5, 275) * mm});
            skLineSegment(sketch, "E142.MirrorCS", {"start": v(364.5, -25) * mm, "end": v(364.5, -5) * mm});
            skLineSegment(sketch, "E143.MirrorCS", {"start": v(364.5, 55) * mm, "end": v(364.5, 75) * mm});
            skLineSegment(sketch, "E144.MirrorCS", {"start": v(364.5, 135) * mm, "end": v(364.5, 155) * mm});
            skLineSegment(sketch, "E145.MirrorCS", {"start": v(367.5, 215) * mm, "end": v(367.5, 235) * mm});
            skLineSegment(sketch, "E146.MirrorCS", {"start": v(367.5, 255) * mm, "end": v(367.5, 275) * mm});
            skLineSegment(sketch, "E147.MirrorCS", {"start": v(367.5, 175) * mm, "end": v(367.5, 195) * mm});
            skLineSegment(sketch, "E148.MirrorCS", {"start": v(364.5, 215) * mm, "end": v(364.5, 235) * mm});
            skLineSegment(sketch, "E149.MirrorCS", {"start": v(367.5, -25) * mm, "end": v(367.5, -5) * mm});
            skLineSegment(sketch, "E150.MirrorCS", {"start": v(367.5, -105) * mm, "end": v(367.5, -85) * mm});
            skLineSegment(sketch, "E151.MirrorCS", {"start": v(367.5, 55) * mm, "end": v(367.5, 75) * mm});
            skLineSegment(sketch, "E152.MirrorCS", {"start": v(367.5, 15) * mm, "end": v(367.5, 35) * mm});
            skLineSegment(sketch, "E153.MirrorCS", {"start": v(367.5, 95) * mm, "end": v(367.5, 115) * mm});
            skLineSegment(sketch, "E154.MirrorCS", {"start": v(364.5, 15) * mm, "end": v(364.5, 35) * mm});
            skLineSegment(sketch, "E155.MirrorCS", {"start": v(364.5, 175) * mm, "end": v(364.5, 195) * mm});
            skLineSegment(sketch, "E156.MirrorCS", {"start": v(445.9, -105) * mm, "end": v(367.5, -105) * mm, "construction": true});
            skLineSegment(sketch, "E157.MirrorCS", {"start": v(477.5, 275) * mm, "end": v(367.5, 275) * mm});
            skLineSegment(sketch, "E158.MirrorCS", {"start": v(477.5, -105) * mm, "end": v(367.5, -105) * mm});
            skLineSegment(sketch, "E159.bottom", {"start": v(387.5, -105) * mm, "end": v(407.5, -105) * mm});
            skLineSegment(sketch, "E159.top", {"start": v(387.5, -108) * mm, "end": v(407.5, -108) * mm});
            skLineSegment(sketch, "E159.left", {"start": v(387.5, -105) * mm, "end": v(387.5, -108) * mm});
            skLineSegment(sketch, "E159.right", {"start": v(407.5, -105) * mm, "end": v(407.5, -108) * mm});
            skLineSegment(sketch, "E160.1.0.0", {"start": v(427.5, -108) * mm, "end": v(447.5, -108) * mm});
            skLineSegment(sketch, "E160.1.0.1", {"start": v(427.5, -105) * mm, "end": v(447.5, -105) * mm});
            skLineSegment(sketch, "E160.1.0.2", {"start": v(427.5, -105) * mm, "end": v(427.5, -108) * mm});
            skLineSegment(sketch, "E160.1.0.3", {"start": v(447.5, -105) * mm, "end": v(447.5, -108) * mm});
            skLineSegment(sketch, "E160.2.0.0", {"start": v(467.5, -108) * mm, "end": v(487.5, -108) * mm});
            skLineSegment(sketch, "E160.2.0.1", {"start": v(467.5, -105) * mm, "end": v(487.5, -105) * mm});
            skLineSegment(sketch, "E160.2.0.2", {"start": v(467.5, -105) * mm, "end": v(467.5, -108) * mm});
            skLineSegment(sketch, "E160.2.0.3", {"start": v(487.5, -105) * mm, "end": v(487.5, -108) * mm});
            skLineSegment(sketch, "E160.3.0.0", {"start": v(507.5, -108) * mm, "end": v(527.5, -108) * mm});
            skLineSegment(sketch, "E160.3.0.1", {"start": v(507.5, -105) * mm, "end": v(527.5, -105) * mm});
            skLineSegment(sketch, "E160.3.0.2", {"start": v(507.5, -105) * mm, "end": v(507.5, -108) * mm});
            skLineSegment(sketch, "E160.3.0.3", {"start": v(527.5, -105) * mm, "end": v(527.5, -108) * mm});
            skLineSegment(sketch, "E160.direction1", {"start": v(387.5, -108) * mm, "end": v(427.5, -108) * mm, "construction": true});
            skLineSegment(sketch, "E161.0.4.0", {"start": v(547.5, -108) * mm, "end": v(567.5, -108) * mm});
            skLineSegment(sketch, "E161.3.4.0", {"start": v(547.5, -105) * mm, "end": v(567.5, -105) * mm});
            skLineSegment(sketch, "E161.6.4.0", {"start": v(547.5, -105) * mm, "end": v(547.5, -108) * mm});
            skLineSegment(sketch, "E161.9.4.0", {"start": v(567.5, -105) * mm, "end": v(567.5, -108) * mm});
            skLineSegment(sketch, "E162.bottom", {"start": v(-199.5, 276) * mm, "end": v(590.5, 276) * mm, "construction": true});
            skLineSegment(sketch, "E162.top", {"start": v(-199.5, -108) * mm, "end": v(590.5, -108) * mm, "construction": true});
            skLineSegment(sketch, "E162.left", {"start": v(-199.5, 276) * mm, "end": v(-199.5, -108) * mm, "construction": true});
            skLineSegment(sketch, "E162.right", {"start": v(590.5, 276) * mm, "end": v(590.5, -108) * mm, "construction": true});
            skLineSegment(sketch, "E163", {"start": v(-116.5, 275) * mm, "end": v(-196.5, 275) * mm});
            skSolve(sketch);
        }
        {
            var Q0;
            Q0=makeQuery(id+"F0.imprint","IMPRINT",FACE,{"disambiguationData":[TD([[makeQuery(id+"F0.imprint","IMPRINT",EDGE,{"derivedFrom":sQuery(id+"F0.wireOp",EDGE,"E2.bottom")}),1.0]])]});
            var Q1;
            Q1=makeQuery(id+"F0.imprint","IMPRINT",FACE,{"disambiguationData":[TD([[makeQuery(id+"F0.imprint","IMPRINT",EDGE,{"derivedFrom":sQuery(id+"F0.wireOp",EDGE,"E3.0.1.0")}),-1.0]])]});
            var Q2;
            Q2=makeQuery(id+"F0.imprint","IMPRINT",FACE,{"disambiguationData":[TD([[makeQuery(id+"F0.imprint","IMPRINT",EDGE,{"derivedFrom":sQuery(id+"F0.wireOp",EDGE,"E3.0.2.0")}),-1.0]])]});
            var Q3;
            Q3=makeQuery(id+"F0.imprint","IMPRINT",FACE,{"disambiguationData":[TD([[makeQuery(id+"F0.imprint","IMPRINT",EDGE,{"derivedFrom":sQuery(id+"F0.wireOp",EDGE,"E3.0.3.0")}),-1.0]])]});
            var Q4;
            Q4=makeQuery(id+"F0.imprint","IMPRINT",FACE,{"disambiguationData":[TD([[makeQuery(id+"F0.imprint","IMPRINT",EDGE,{"derivedFrom":sQuery(id+"F0.wireOp",EDGE,"E3.0.4.0")}),-1.0]])]});
            var Q5;
            Q5=makeQuery(id+"F0.imprint","IMPRINT",FACE,{"disambiguationData":[TD([[makeQuery(id+"F0.imprint","IMPRINT",EDGE,{"derivedFrom":sQuery(id+"F0.wireOp",EDGE,"E3.0.5.0")}),-1.0]])]});
            var Q6;
            Q6=makeQuery(id+"F0.imprint","IMPRINT",FACE,{"disambiguationData":[TD([[makeQuery(id+"F0.imprint","IMPRINT",EDGE,{"derivedFrom":sQuery(id+"F0.wireOp",EDGE,"E3.0.6.0")}),-1.0]])]});
            var Q7;
            Q7=makeQuery(id+"F0.imprint","IMPRINT",FACE,{"disambiguationData":[TD([[makeQuery(id+"F0.imprint","IMPRINT",EDGE,{"derivedFrom":sQuery(id+"F0.wireOp",EDGE,"E3.0.7.0")}),-1.0]])]});
            var Q8;
            Q8=makeQuery(id+"F0.imprint","IMPRINT",FACE,{"disambiguationData":[TD([[makeQuery(id+"F0.imprint","IMPRINT",EDGE,{"derivedFrom":sQuery(id+"F0.wireOp",EDGE,"E3.0.8.0")}),-1.0]])]});
            var Q9;
            Q9=makeQuery(id+"F0.imprint","IMPRINT",FACE,{"disambiguationData":[TD([[makeQuery(id+"F0.imprint","IMPRINT",EDGE,{"derivedFrom":sQuery(id+"F0.wireOp",EDGE,"E3.0.9.0")}),-1.0]])]});
            var Q10;
            Q10=makeQuery(id+"F0.imprint","IMPRINT",FACE,{"disambiguationData":[TD([[makeQuery(id+"F0.imprint","IMPRINT",EDGE,{"derivedFrom":sQuery(id+"F0.wireOp",EDGE,"f4fa3369-b130-4f32-bb59-d94157c80696.0.0.10")}),-1.0]])]});
            var Q11;
            Q11=makeQuery(id+"F0.imprint","IMPRINT",FACE,{"disambiguationData":[TD([[makeQuery(id+"F0.imprint","IMPRINT",EDGE,{"derivedFrom":sQuery(id+"F0.wireOp",EDGE,"f4fa3369-b130-4f32-bb59-d94157c80696.0.0.11")}),-1.0]])]});
            var Q12;
            Q12=makeQuery(id+"F0.imprint","IMPRINT",FACE,{"disambiguationData":[TD([[makeQuery(id+"F0.imprint","IMPRINT",EDGE,{"derivedFrom":sQuery(id+"F0.wireOp",EDGE,"f4fa3369-b130-4f32-bb59-d94157c80696.0.0.12")}),-1.0]])]});
            var Q13;
            Q13=makeQuery(id+"F0.imprint","IMPRINT",FACE,{"disambiguationData":[TD([[makeQuery(id+"F0.imprint","IMPRINT",EDGE,{"derivedFrom":sQuery(id+"F0.wireOp",EDGE,"f4fa3369-b130-4f32-bb59-d94157c80696.0.0.13")}),-1.0]])]});
            var Q14;
            Q14=makeQuery(id+"F0.imprint","IMPRINT",FACE,{"disambiguationData":[TD([[makeQuery(id+"F0.imprint","IMPRINT",EDGE,{"derivedFrom":sQuery(id+"F0.wireOp",EDGE,"E4.MirrorCS")}),-1.0]])]});
            var Q15;
            Q15=makeQuery(id+"F0.imprint","IMPRINT",FACE,{"disambiguationData":[TD([[makeQuery(id+"F0.imprint","IMPRINT",EDGE,{"derivedFrom":sQuery(id+"F0.wireOp",EDGE,"2ae0f608-4d21-4aad-a97f-9b663aa70c851.MirrorCS")}),1.0]])]});
            var Q16;
            Q16=makeQuery(id+"F0.imprint","IMPRINT",FACE,{"disambiguationData":[TD([[makeQuery(id+"F0.imprint","IMPRINT",EDGE,{"derivedFrom":sQuery(id+"F0.wireOp",EDGE,"E5.MirrorCS")}),-1.0]])]});
            var Q17;
            Q17=makeQuery(id+"F0.imprint","IMPRINT",FACE,{"disambiguationData":[TD([[makeQuery(id+"F0.imprint","IMPRINT",EDGE,{"derivedFrom":sQuery(id+"F0.wireOp",EDGE,"2ae0f608-4d21-4aad-a97f-9b663aa70c853.MirrorCS")}),-1.0]])]});
            var Q18;
            Q18=makeQuery(id+"F0.imprint","IMPRINT",FACE,{"disambiguationData":[TD([[makeQuery(id+"F0.imprint","IMPRINT",EDGE,{"derivedFrom":sQuery(id+"F0.wireOp",EDGE,"2ae0f608-4d21-4aad-a97f-9b663aa70c854.MirrorCS")}),-1.0]])]});
            var Q19;
            Q19=makeQuery(id+"F0.imprint","IMPRINT",FACE,{"disambiguationData":[TD([[makeQuery(id+"F0.imprint","IMPRINT",EDGE,{"derivedFrom":sQuery(id+"F0.wireOp",EDGE,"E8.MirrorCS")}),1.0]])]});
            var Q20;
            Q20=makeQuery(id+"F0.imprint","IMPRINT",FACE,{"disambiguationData":[TD([[makeQuery(id+"F0.imprint","IMPRINT",EDGE,{"derivedFrom":sQuery(id+"F0.wireOp",EDGE,"E9.MirrorCS")}),1.0]])]});
            var Q21;
            {var subQ0=sQuery(id+"F0.wireOp",EDGE,"E10.MirrorCS");Q21=makeQuery(id+"F0.imprint","IMPRINT",FACE,{"disambiguationData":[TD([[makeQuery(id+"F0.imprint","IMPRINT",EDGE,{"derivedFrom":subQ0}),1.0]])]});}
            var Q22;
            Q22=makeQuery(id+"F0.imprint","IMPRINT",FACE,{"disambiguationData":[TD([[makeQuery(id+"F0.imprint","IMPRINT",EDGE,{"derivedFrom":sQuery(id+"F0.wireOp",EDGE,"E11.MirrorCS")}),1.0]])]});
            var Q23;
            {var subQ0=sQuery(id+"F0.wireOp",EDGE,"E12.MirrorCS");Q23=makeQuery(id+"F0.imprint","IMPRINT",FACE,{"disambiguationData":[TD([[makeQuery(id+"F0.imprint","IMPRINT",EDGE,{"derivedFrom":subQ0}),1.0]])]});}
            var Q24;
            Q24=makeQuery(id+"F0.imprint","IMPRINT",FACE,{"disambiguationData":[TD([[makeQuery(id+"F0.imprint","IMPRINT",EDGE,{"derivedFrom":sQuery(id+"F0.wireOp",EDGE,"E17.MirrorCS")}),1.0]])]});
            var Q25;
            Q25=makeQuery(id+"F0.imprint","IMPRINT",FACE,{"disambiguationData":[TD([[makeQuery(id+"F0.imprint","IMPRINT",EDGE,{"derivedFrom":sQuery(id+"F0.wireOp",EDGE,"E18.MirrorCS")}),1.0]])]});
            var Q26;
            Q26=makeQuery(id+"F0.imprint","IMPRINT",FACE,{"disambiguationData":[TD([[makeQuery(id+"F0.imprint","IMPRINT",EDGE,{"derivedFrom":sQuery(id+"F0.wireOp",EDGE,"2ae0f608-4d21-4aad-a97f-9b663aa70c8519.MirrorCS")}),-1.0]])]});
            var Q27;
            Q27=makeQuery(id+"F0.imprint","IMPRINT",FACE,{"disambiguationData":[TD([[makeQuery(id+"F0.imprint","IMPRINT",EDGE,{"derivedFrom":sQuery(id+"F0.wireOp",EDGE,"E21.MirrorCS")}),1.0]])]});
            var Q28;
            {var subQ23=sQuery(id+"F0.wireOp",EDGE,"E1.top");Q28=makeQuery(id+"F0.imprint","IMPRINT",FACE,{"disambiguationData":[TD([[makeQuery(id+"F0.imprint","IMPRINT",EDGE,{"derivedFrom":subQ23}),-1.0]])]});}
            var Q29;
            {var subQ9=sQuery(id+"F0.wireOp",EDGE,"E97.MirrorCS");Q29=makeQuery(id+"F0.imprint","IMPRINT",FACE,{"disambiguationData":[TD([[makeQuery(id+"F0.imprint","IMPRINT",EDGE,{"derivedFrom":subQ9}),1.0]])]});}
            var Q30;
            Q30=makeQuery(id+"F0.imprint","IMPRINT",FACE,{"disambiguationData":[TD([[makeQuery(id+"F0.imprint","IMPRINT",EDGE,{"derivedFrom":sQuery(id+"F0.wireOp",EDGE,"E51.0.5.0")}),-1.0]])]});
            var Q31;
            Q31=makeQuery(id+"F0.imprint","IMPRINT",FACE,{"disambiguationData":[TD([[makeQuery(id+"F0.imprint","IMPRINT",EDGE,{"derivedFrom":sQuery(id+"F0.wireOp",EDGE,"75591c1a-0551-4687-a083-02fff30de030.0.0.10")}),-1.0]])]});
            var Q32;
            {var subQ0=sQuery(id+"F0.wireOp",EDGE,"E78.MirrorCS");Q32=makeQuery(id+"F0.imprint","IMPRINT",FACE,{"disambiguationData":[TD([[makeQuery(id+"F0.imprint","IMPRINT",EDGE,{"derivedFrom":subQ0}),-1.0]])]});}
            var Q33;
            {var subQ0=sQuery(id+"F0.wireOp",EDGE,"19c01f95-d842-4a0e-ad16-a6d598b7f029.MirrorCS");Q33=makeQuery(id+"F0.imprint","IMPRINT",FACE,{"disambiguationData":[TD([[makeQuery(id+"F0.imprint","IMPRINT",EDGE,{"derivedFrom":subQ0}),1.0]])]});}
            var Q34;
            Q34=makeQuery(id+"F0.imprint","IMPRINT",FACE,{"disambiguationData":[TD([[makeQuery(id+"F0.imprint","IMPRINT",EDGE,{"derivedFrom":sQuery(id+"F0.wireOp",EDGE,"E51.0.7.0")}),-1.0]])]});
            var Q35;
            Q35=makeQuery(id+"F0.imprint","IMPRINT",FACE,{"disambiguationData":[TD([[makeQuery(id+"F0.imprint","IMPRINT",EDGE,{"derivedFrom":sQuery(id+"F0.wireOp",EDGE,"75591c1a-0551-4687-a083-02fff30de030.0.0.11")}),-1.0]])]});
            var Q36;
            Q36=makeQuery(id+"F0.imprint","IMPRINT",FACE,{"disambiguationData":[TD([[makeQuery(id+"F0.imprint","IMPRINT",EDGE,{"derivedFrom":sQuery(id+"F0.wireOp",EDGE,"E51.0.4.0")}),-1.0]])]});
            var Q37;
            Q37=makeQuery(id+"F0.imprint","IMPRINT",FACE,{"disambiguationData":[TD([[makeQuery(id+"F0.imprint","IMPRINT",EDGE,{"derivedFrom":sQuery(id+"F0.wireOp",EDGE,"E51.0.6.0")}),-1.0]])]});
            var Q38;
            Q38=makeQuery(id+"F0.imprint","IMPRINT",FACE,{"disambiguationData":[TD([[makeQuery(id+"F0.imprint","IMPRINT",EDGE,{"derivedFrom":sQuery(id+"F0.wireOp",EDGE,"E51.0.8.0")}),-1.0]])]});
            var Q39;
            Q39=makeQuery(id+"F0.imprint","IMPRINT",FACE,{"disambiguationData":[TD([[makeQuery(id+"F0.imprint","IMPRINT",EDGE,{"derivedFrom":sQuery(id+"F0.wireOp",EDGE,"E51.0.1.0")}),-1.0]])]});
            var Q40;
            Q40=makeQuery(id+"F0.imprint","IMPRINT",FACE,{"disambiguationData":[TD([[makeQuery(id+"F0.imprint","IMPRINT",EDGE,{"derivedFrom":sQuery(id+"F0.wireOp",EDGE,"75591c1a-0551-4687-a083-02fff30de030.0.0.12")}),-1.0]])]});
            var Q41;
            Q41=makeQuery(id+"F0.imprint","IMPRINT",FACE,{"disambiguationData":[TD([[makeQuery(id+"F0.imprint","IMPRINT",EDGE,{"derivedFrom":sQuery(id+"F0.wireOp",EDGE,"75591c1a-0551-4687-a083-02fff30de030.0.0.13")}),-1.0]])]});
            var Q42;
            Q42=makeQuery(id+"F0.imprint","IMPRINT",FACE,{"disambiguationData":[TD([[makeQuery(id+"F0.imprint","IMPRINT",EDGE,{"derivedFrom":sQuery(id+"F0.wireOp",EDGE,"E51.0.3.0")}),-1.0]])]});
            var Q43;
            Q43=makeQuery(id+"F0.imprint","IMPRINT",FACE,{"disambiguationData":[TD([[makeQuery(id+"F0.imprint","IMPRINT",EDGE,{"derivedFrom":sQuery(id+"F0.wireOp",EDGE,"E51.0.9.0")}),-1.0]])]});
            var Q44;
            Q44=makeQuery(id+"F0.imprint","IMPRINT",FACE,{"disambiguationData":[TD([[makeQuery(id+"F0.imprint","IMPRINT",EDGE,{"derivedFrom":sQuery(id+"F0.wireOp",EDGE,"E51.0.2.0")}),-1.0]])]});
            var Q45;
            {var subQ0=sQuery(id+"F0.wireOp",EDGE,"E69.MirrorCS");Q45=makeQuery(id+"F0.imprint","IMPRINT",FACE,{"disambiguationData":[TD([[makeQuery(id+"F0.imprint","IMPRINT",EDGE,{"derivedFrom":subQ0}),1.0]])]});}
            var Q46;
            {var subQ0=sQuery(id+"F0.wireOp",EDGE,"E79.MirrorCS");Q46=makeQuery(id+"F0.imprint","IMPRINT",FACE,{"disambiguationData":[TD([[makeQuery(id+"F0.imprint","IMPRINT",EDGE,{"derivedFrom":subQ0}),-1.0]])]});}
            var Q47;
            {var subQ0=sQuery(id+"F0.wireOp",EDGE,"E62.MirrorCS");Q47=makeQuery(id+"F0.imprint","IMPRINT",FACE,{"disambiguationData":[TD([[makeQuery(id+"F0.imprint","IMPRINT",EDGE,{"derivedFrom":subQ0}),-1.0]])]});}
            var Q48;
            Q48=makeQuery(id+"F0.imprint","IMPRINT",FACE,{"disambiguationData":[TD([[makeQuery(id+"F0.imprint","IMPRINT",EDGE,{"derivedFrom":sQuery(id+"F0.wireOp",EDGE,"7f64ed7e-c29e-4442-a259-6be69fc43930.MirrorCS")}),-1.0]])]});
            var Q49;
            Q49=makeQuery(id+"F0.imprint","IMPRINT",FACE,{"disambiguationData":[TD([[makeQuery(id+"F0.imprint","IMPRINT",EDGE,{"derivedFrom":sQuery(id+"F0.wireOp",EDGE,"E65.MirrorCS")}),-1.0]])]});
            var Q50;
            {var subQ0=sQuery(id+"F0.wireOp",EDGE,"E61.MirrorCS");Q50=makeQuery(id+"F0.imprint","IMPRINT",FACE,{"disambiguationData":[TD([[makeQuery(id+"F0.imprint","IMPRINT",EDGE,{"derivedFrom":subQ0}),-1.0]])]});}
            var Q51;
            {var subQ0=sQuery(id+"F0.wireOp",EDGE,"E58.MirrorCS");Q51=makeQuery(id+"F0.imprint","IMPRINT",FACE,{"disambiguationData":[TD([[makeQuery(id+"F0.imprint","IMPRINT",EDGE,{"derivedFrom":subQ0}),-1.0]])]});}
            var Q52;
            {var subQ0=sQuery(id+"F0.wireOp",EDGE,"377e4eac-6a3e-45b7-abb5-2cd0d814bb82.MirrorCS");Q52=makeQuery(id+"F0.imprint","IMPRINT",FACE,{"disambiguationData":[TD([[makeQuery(id+"F0.imprint","IMPRINT",EDGE,{"derivedFrom":subQ0}),-1.0]])]});}
            var Q53;
            {var subQ0=sQuery(id+"F0.wireOp",EDGE,"E77.MirrorCS");Q53=makeQuery(id+"F0.imprint","IMPRINT",FACE,{"disambiguationData":[TD([[makeQuery(id+"F0.imprint","IMPRINT",EDGE,{"derivedFrom":subQ0}),1.0]])]});}
            var Q54;
            {var subQ0=sQuery(id+"F0.wireOp",EDGE,"431cc23e-2807-4637-a186-def6c824f336.MirrorCS");Q54=makeQuery(id+"F0.imprint","IMPRINT",FACE,{"disambiguationData":[TD([[makeQuery(id+"F0.imprint","IMPRINT",EDGE,{"derivedFrom":subQ0}),-1.0]])]});}
            var Q55;
            Q55=makeQuery(id+"F0.imprint","IMPRINT",FACE,{"disambiguationData":[TD([[makeQuery(id+"F0.imprint","IMPRINT",EDGE,{"derivedFrom":sQuery(id+"F0.wireOp",EDGE,"E74.MirrorCS")}),-1.0]])]});
            var Q56;
            {var subQ3=sQuery(id+"F0.wireOp",EDGE,"E51.0.1.0");Q56=makeQuery(id+"F0.imprint","IMPRINT",FACE,{"disambiguationData":[TD([[makeQuery(id+"F0.imprint","IMPRINT",EDGE,{"derivedFrom":subQ3}),1.0]])]});}
            var Q57;
            {var subQ5=sQuery(id+"F0.wireOp",EDGE,"E103.right");Q57=makeQuery(id+"F0.imprint","IMPRINT",FACE,{"disambiguationData":[TD([[makeQuery(id+"F0.imprint","IMPRINT",EDGE,{"derivedFrom":subQ5}),-1.0]])]});}
            var Q58;
            {var subQ5=sQuery(id+"F0.wireOp",EDGE,"E103.left");Q58=makeQuery(id+"F0.imprint","IMPRINT",FACE,{"disambiguationData":[TD([[makeQuery(id+"F0.imprint","IMPRINT",EDGE,{"derivedFrom":subQ5}),1.0]])]});}
            var Q59;
            {var subQ3=sQuery(id+"F0.wireOp",EDGE,"E106.bottom");Q59=makeQuery(id+"F0.imprint","IMPRINT",FACE,{"disambiguationData":[TD([[makeQuery(id+"F0.imprint","IMPRINT",EDGE,{"derivedFrom":subQ3}),-1.0]])]});}
            var Q60;
            Q60=makeQuery(id+"F0.imprint","IMPRINT",FACE,{"disambiguationData":[TD([[makeQuery(id+"F0.imprint","IMPRINT",EDGE,{"derivedFrom":sQuery(id+"F0.wireOp",EDGE,"E107.2.1.0")}),-1.0]])]});
            var Q61;
            Q61=makeQuery(id+"F0.imprint","IMPRINT",FACE,{"disambiguationData":[TD([[makeQuery(id+"F0.imprint","IMPRINT",EDGE,{"derivedFrom":sQuery(id+"F0.wireOp",EDGE,"E107.3.1.0")}),-1.0]])]});
            var Q62;
            Q62=makeQuery(id+"F0.imprint","IMPRINT",FACE,{"disambiguationData":[TD([[makeQuery(id+"F0.imprint","IMPRINT",EDGE,{"derivedFrom":sQuery(id+"F0.wireOp",EDGE,"E107.4.1.0")}),-1.0]])]});
            var Q63;
            Q63=makeQuery(id+"F0.imprint","IMPRINT",FACE,{"disambiguationData":[TD([[makeQuery(id+"F0.imprint","IMPRINT",EDGE,{"derivedFrom":sQuery(id+"F0.wireOp",EDGE,"E107.1.1.0")}),-1.0]])]});
            var Q64;
            Q64=makeQuery(id+"F0.imprint","IMPRINT",FACE,{"disambiguationData":[TD([[makeQuery(id+"F0.imprint","IMPRINT",EDGE,{"derivedFrom":sQuery(id+"F0.wireOp",EDGE,"E107.0.1.0")}),-1.0]])]});
            var Q65;
            Q65=makeQuery(id+"F0.imprint","IMPRINT",FACE,{"disambiguationData":[TD([[makeQuery(id+"F0.imprint","IMPRINT",EDGE,{"derivedFrom":sQuery(id+"F0.wireOp",EDGE,"E107.5.1.0")}),-1.0]])]});
            var Q66;
            Q66=makeQuery(id+"F0.imprint","IMPRINT",FACE,{"disambiguationData":[TD([[makeQuery(id+"F0.imprint","IMPRINT",EDGE,{"derivedFrom":sQuery(id+"F0.wireOp",EDGE,"E109.bottom")}),-1.0]])]});
            var Q67;
            Q67=makeQuery(id+"F0.imprint","IMPRINT",FACE,{"disambiguationData":[TD([[makeQuery(id+"F0.imprint","IMPRINT",EDGE,{"derivedFrom":sQuery(id+"F0.wireOp",EDGE,"E107.2.0.0")}),-1.0]])]});
            var Q68;
            Q68=makeQuery(id+"F0.imprint","IMPRINT",FACE,{"disambiguationData":[TD([[makeQuery(id+"F0.imprint","IMPRINT",EDGE,{"derivedFrom":sQuery(id+"F0.wireOp",EDGE,"E107.3.0.0")}),-1.0]])]});
            var Q69;
            Q69=makeQuery(id+"F0.imprint","IMPRINT",FACE,{"disambiguationData":[TD([[makeQuery(id+"F0.imprint","IMPRINT",EDGE,{"derivedFrom":sQuery(id+"F0.wireOp",EDGE,"E107.4.0.0")}),-1.0]])]});
            var Q70;
            Q70=makeQuery(id+"F0.imprint","IMPRINT",FACE,{"disambiguationData":[TD([[makeQuery(id+"F0.imprint","IMPRINT",EDGE,{"derivedFrom":sQuery(id+"F0.wireOp",EDGE,"E107.5.0.0")}),-1.0]])]});
            var Q71;
            Q71=makeQuery(id+"F0.imprint","IMPRINT",FACE,{"disambiguationData":[TD([[makeQuery(id+"F0.imprint","IMPRINT",EDGE,{"derivedFrom":sQuery(id+"F0.wireOp",EDGE,"E106.bottom")}),1.0]])]});
            var Q72;
            Q72=makeQuery(id+"F0.imprint","IMPRINT",FACE,{"disambiguationData":[TD([[makeQuery(id+"F0.imprint","IMPRINT",EDGE,{"derivedFrom":sQuery(id+"F0.wireOp",EDGE,"E108.bottom")}),1.0]])]});
            var Q73;
            Q73=makeQuery(id+"F0.imprint","IMPRINT",FACE,{"disambiguationData":[TD([[makeQuery(id+"F0.imprint","IMPRINT",EDGE,{"derivedFrom":sQuery(id+"F0.wireOp",EDGE,"E107.1.0.0")}),-1.0]])]});
            var Q74;
            Q74=makeQuery(id+"F0.imprint","IMPRINT",FACE,{"disambiguationData":[TD([[makeQuery(id+"F0.imprint","IMPRINT",EDGE,{"derivedFrom":sQuery(id+"F0.wireOp",EDGE,"E101.3.0.0")}),1.0]])]});
            var Q75;
            Q75=makeQuery(id+"F0.imprint","IMPRINT",FACE,{"disambiguationData":[TD([[makeQuery(id+"F0.imprint","IMPRINT",EDGE,{"derivedFrom":sQuery(id+"F0.wireOp",EDGE,"E102.0.4.0")}),1.0]])]});
            var Q76;
            Q76=makeQuery(id+"F0.imprint","IMPRINT",FACE,{"disambiguationData":[TD([[makeQuery(id+"F0.imprint","IMPRINT",EDGE,{"derivedFrom":sQuery(id+"F0.wireOp",EDGE,"E100.bottom")}),-1.0]])]});
            var Q77;
            Q77=makeQuery(id+"F0.imprint","IMPRINT",FACE,{"disambiguationData":[TD([[makeQuery(id+"F0.imprint","IMPRINT",EDGE,{"derivedFrom":sQuery(id+"F0.wireOp",EDGE,"E101.1.0.0")}),1.0]])]});
            var Q78;
            Q78=makeQuery(id+"F0.imprint","IMPRINT",FACE,{"disambiguationData":[TD([[makeQuery(id+"F0.imprint","IMPRINT",EDGE,{"derivedFrom":sQuery(id+"F0.wireOp",EDGE,"E101.2.0.0")}),1.0]])]});
            var Q79;
            {var subQ5=sQuery(id+"F0.wireOp",EDGE,"E104.right");Q79=makeQuery(id+"F0.imprint","IMPRINT",FACE,{"disambiguationData":[TD([[makeQuery(id+"F0.imprint","IMPRINT",EDGE,{"derivedFrom":subQ5}),1.0]])]});}
            var Q80;
            {var subQ5=sQuery(id+"F0.wireOp",EDGE,"E104.left");Q80=makeQuery(id+"F0.imprint","IMPRINT",FACE,{"disambiguationData":[TD([[makeQuery(id+"F0.imprint","IMPRINT",EDGE,{"derivedFrom":subQ5}),-1.0]])]});}
            var Q81;
            {var subQ8=sQuery(id+"F0.wireOp",EDGE,"E35.MirrorCS");Q81=makeQuery(id+"F0.imprint","IMPRINT",FACE,{"disambiguationData":[TD([[makeQuery(id+"F0.imprint","IMPRINT",EDGE,{"derivedFrom":subQ8}),-1.0]])]});}
            var Q82;
            {var subQ3=sQuery(id+"F0.wireOp",EDGE,"E145.MirrorCS");Q82=makeQuery(id+"F0.imprint","IMPRINT",FACE,{"disambiguationData":[TD([[makeQuery(id+"F0.imprint","IMPRINT",EDGE,{"derivedFrom":subQ3}),-1.0]])]});}
            var Q83;
            {var subQ24=sQuery(id+"F0.wireOp",EDGE,"E111.top");Q83=makeQuery(id+"F0.imprint","IMPRINT",FACE,{"disambiguationData":[TD([[makeQuery(id+"F0.imprint","IMPRINT",EDGE,{"derivedFrom":subQ24}),-1.0]])]});}
            var Q84;
            Q84=makeQuery(id+"F0.imprint","IMPRINT",FACE,{"disambiguationData":[TD([[makeQuery(id+"F0.imprint","IMPRINT",EDGE,{"derivedFrom":sQuery(id+"F0.wireOp",EDGE,"E127.MirrorCS")}),1.0]])]});
            var Q85;
            Q85=makeQuery(id+"F0.imprint","IMPRINT",FACE,{"disambiguationData":[TD([[makeQuery(id+"F0.imprint","IMPRINT",EDGE,{"derivedFrom":sQuery(id+"F0.wireOp",EDGE,"6c8e19b1-94a5-4b05-b23f-bae359994a46.MirrorCS")}),-1.0]])]});
            var Q86;
            Q86=makeQuery(id+"F0.imprint","IMPRINT",FACE,{"disambiguationData":[TD([[makeQuery(id+"F0.imprint","IMPRINT",EDGE,{"derivedFrom":sQuery(id+"F0.wireOp",EDGE,"E119.MirrorCS")}),1.0]])]});
            var Q87;
            Q87=makeQuery(id+"F0.imprint","IMPRINT",FACE,{"disambiguationData":[TD([[makeQuery(id+"F0.imprint","IMPRINT",EDGE,{"derivedFrom":sQuery(id+"F0.wireOp",EDGE,"E131.MirrorCS")}),1.0]])]});
            var Q88;
            Q88=makeQuery(id+"F0.imprint","IMPRINT",FACE,{"disambiguationData":[TD([[makeQuery(id+"F0.imprint","IMPRINT",EDGE,{"derivedFrom":sQuery(id+"F0.wireOp",EDGE,"E113.0.4.0")}),-1.0]])]});
            var Q89;
            Q89=makeQuery(id+"F0.imprint","IMPRINT",FACE,{"disambiguationData":[TD([[makeQuery(id+"F0.imprint","IMPRINT",EDGE,{"derivedFrom":sQuery(id+"F0.wireOp",EDGE,"49f08d63-0267-40d7-bac4-a3968ec503cd.0.0.12")}),-1.0]])]});
            var Q90;
            Q90=makeQuery(id+"F0.imprint","IMPRINT",FACE,{"disambiguationData":[TD([[makeQuery(id+"F0.imprint","IMPRINT",EDGE,{"derivedFrom":sQuery(id+"F0.wireOp",EDGE,"E159.bottom")}),-1.0]])]});
            var Q91;
            Q91=makeQuery(id+"F0.imprint","IMPRINT",FACE,{"disambiguationData":[TD([[makeQuery(id+"F0.imprint","IMPRINT",EDGE,{"derivedFrom":sQuery(id+"F0.wireOp",EDGE,"E160.1.0.0")}),1.0]])]});
            var Q92;
            Q92=makeQuery(id+"F0.imprint","IMPRINT",FACE,{"disambiguationData":[TD([[makeQuery(id+"F0.imprint","IMPRINT",EDGE,{"derivedFrom":sQuery(id+"F0.wireOp",EDGE,"E160.3.0.0")}),1.0]])]});
            var Q93;
            Q93=makeQuery(id+"F0.imprint","IMPRINT",FACE,{"disambiguationData":[TD([[makeQuery(id+"F0.imprint","IMPRINT",EDGE,{"derivedFrom":sQuery(id+"F0.wireOp",EDGE,"E112.bottom")}),1.0]])]});
            var Q94;
            Q94=makeQuery(id+"F0.imprint","IMPRINT",FACE,{"disambiguationData":[TD([[makeQuery(id+"F0.imprint","IMPRINT",EDGE,{"derivedFrom":sQuery(id+"F0.wireOp",EDGE,"E113.0.9.0")}),-1.0]])]});
            var Q95;
            Q95=makeQuery(id+"F0.imprint","IMPRINT",FACE,{"disambiguationData":[TD([[makeQuery(id+"F0.imprint","IMPRINT",EDGE,{"derivedFrom":sQuery(id+"F0.wireOp",EDGE,"E113.0.7.0")}),-1.0]])]});
            var Q96;
            Q96=makeQuery(id+"F0.imprint","IMPRINT",FACE,{"disambiguationData":[TD([[makeQuery(id+"F0.imprint","IMPRINT",EDGE,{"derivedFrom":sQuery(id+"F0.wireOp",EDGE,"49f08d63-0267-40d7-bac4-a3968ec503cd.0.0.10")}),-1.0]])]});
            var Q97;
            Q97=makeQuery(id+"F0.imprint","IMPRINT",FACE,{"disambiguationData":[TD([[makeQuery(id+"F0.imprint","IMPRINT",EDGE,{"derivedFrom":sQuery(id+"F0.wireOp",EDGE,"E113.0.6.0")}),-1.0]])]});
            var Q98;
            Q98=makeQuery(id+"F0.imprint","IMPRINT",FACE,{"disambiguationData":[TD([[makeQuery(id+"F0.imprint","IMPRINT",EDGE,{"derivedFrom":sQuery(id+"F0.wireOp",EDGE,"49f08d63-0267-40d7-bac4-a3968ec503cd.0.0.13")}),-1.0]])]});
            var Q99;
            Q99=makeQuery(id+"F0.imprint","IMPRINT",FACE,{"disambiguationData":[TD([[makeQuery(id+"F0.imprint","IMPRINT",EDGE,{"derivedFrom":sQuery(id+"F0.wireOp",EDGE,"E161.0.4.0")}),1.0]])]});
            var Q100;
            Q100=makeQuery(id+"F0.imprint","IMPRINT",FACE,{"disambiguationData":[TD([[makeQuery(id+"F0.imprint","IMPRINT",EDGE,{"derivedFrom":sQuery(id+"F0.wireOp",EDGE,"0c9e000d-f173-4831-abcf-e33b76fcf227.MirrorCS")}),1.0]])]});
            var Q101;
            Q101=makeQuery(id+"F0.imprint","IMPRINT",FACE,{"disambiguationData":[TD([[makeQuery(id+"F0.imprint","IMPRINT",EDGE,{"derivedFrom":sQuery(id+"F0.wireOp",EDGE,"E113.0.1.0")}),-1.0]])]});
            var Q102;
            Q102=makeQuery(id+"F0.imprint","IMPRINT",FACE,{"disambiguationData":[TD([[makeQuery(id+"F0.imprint","IMPRINT",EDGE,{"derivedFrom":sQuery(id+"F0.wireOp",EDGE,"430903dc-0179-4879-afe8-f240adc6c4ab.MirrorCS")}),-1.0]])]});
            var Q103;
            Q103=makeQuery(id+"F0.imprint","IMPRINT",FACE,{"disambiguationData":[TD([[makeQuery(id+"F0.imprint","IMPRINT",EDGE,{"derivedFrom":sQuery(id+"F0.wireOp",EDGE,"E118.MirrorCS")}),1.0]])]});
            var Q104;
            Q104=makeQuery(id+"F0.imprint","IMPRINT",FACE,{"disambiguationData":[TD([[makeQuery(id+"F0.imprint","IMPRINT",EDGE,{"derivedFrom":sQuery(id+"F0.wireOp",EDGE,"E128.MirrorCS")}),1.0]])]});
            var Q105;
            {var subQ0=sQuery(id+"F0.wireOp",EDGE,"E122.MirrorCS");Q105=makeQuery(id+"F0.imprint","IMPRINT",FACE,{"disambiguationData":[TD([[makeQuery(id+"F0.imprint","IMPRINT",EDGE,{"derivedFrom":subQ0}),1.0]])]});}
            var Q106;
            Q106=makeQuery(id+"F0.imprint","IMPRINT",FACE,{"disambiguationData":[TD([[makeQuery(id+"F0.imprint","IMPRINT",EDGE,{"derivedFrom":sQuery(id+"F0.wireOp",EDGE,"E113.0.5.0")}),-1.0]])]});
            var Q107;
            Q107=makeQuery(id+"F0.imprint","IMPRINT",FACE,{"disambiguationData":[TD([[makeQuery(id+"F0.imprint","IMPRINT",EDGE,{"derivedFrom":sQuery(id+"F0.wireOp",EDGE,"49f08d63-0267-40d7-bac4-a3968ec503cd.0.0.11")}),-1.0]])]});
            var Q108;
            Q108=makeQuery(id+"F0.imprint","IMPRINT",FACE,{"disambiguationData":[TD([[makeQuery(id+"F0.imprint","IMPRINT",EDGE,{"derivedFrom":sQuery(id+"F0.wireOp",EDGE,"E115.MirrorCS")}),-1.0]])]});
            var Q109;
            Q109=makeQuery(id+"F0.imprint","IMPRINT",FACE,{"disambiguationData":[TD([[makeQuery(id+"F0.imprint","IMPRINT",EDGE,{"derivedFrom":sQuery(id+"F0.wireOp",EDGE,"E113.0.2.0")}),-1.0]])]});
            var Q110;
            Q110=makeQuery(id+"F0.imprint","IMPRINT",FACE,{"disambiguationData":[TD([[makeQuery(id+"F0.imprint","IMPRINT",EDGE,{"derivedFrom":sQuery(id+"F0.wireOp",EDGE,"E121.MirrorCS")}),1.0]])]});
            var Q111;
            Q111=makeQuery(id+"F0.imprint","IMPRINT",FACE,{"disambiguationData":[TD([[makeQuery(id+"F0.imprint","IMPRINT",EDGE,{"derivedFrom":sQuery(id+"F0.wireOp",EDGE,"E113.0.3.0")}),-1.0]])]});
            var Q112;
            {var subQ0=sQuery(id+"F0.wireOp",EDGE,"E120.MirrorCS");Q112=makeQuery(id+"F0.imprint","IMPRINT",FACE,{"disambiguationData":[TD([[makeQuery(id+"F0.imprint","IMPRINT",EDGE,{"derivedFrom":subQ0}),1.0]])]});}
            var Q113;
            Q113=makeQuery(id+"F0.imprint","IMPRINT",FACE,{"disambiguationData":[TD([[makeQuery(id+"F0.imprint","IMPRINT",EDGE,{"derivedFrom":sQuery(id+"F0.wireOp",EDGE,"E160.2.0.0")}),1.0]])]});
            var Q114;
            Q114=makeQuery(id+"F0.imprint","IMPRINT",FACE,{"disambiguationData":[TD([[makeQuery(id+"F0.imprint","IMPRINT",EDGE,{"derivedFrom":sQuery(id+"F0.wireOp",EDGE,"E113.0.8.0")}),-1.0]])]});
            var Q115;
            Q115=makeQuery(id+"F0.imprint","IMPRINT",FACE,{"disambiguationData":[TD([[makeQuery(id+"F0.imprint","IMPRINT",EDGE,{"derivedFrom":sQuery(id+"F0.wireOp",EDGE,"E114.MirrorCS")}),-1.0]])]});
            var Q116;
            Q116=makeQuery(id+"F0.imprint","IMPRINT",FACE,{"disambiguationData":[TD([[makeQuery(id+"F0.imprint","IMPRINT",EDGE,{"derivedFrom":sQuery(id+"F0.wireOp",EDGE,"baf3ac46-7904-4b15-9d03-7429fad6715b.MirrorCS")}),-1.0]])]});
            extrude(context, id + "F1", {"entities" : qUnion([Q0, Q1, Q2, Q3, Q4, Q5, Q6, Q7, Q8, Q9, Q10, Q11, Q12, Q13, Q14, Q15, Q16, Q17, Q18, Q19, Q20, Q21, Q22, Q23, Q24, Q25, Q26, Q27, Q28, Q29, Q30, Q31, Q32, Q33, Q34, Q35, Q36, Q37, Q38, Q39, Q40, Q41, Q42, Q43, Q44, Q45, Q46, Q47, Q48, Q49, Q50, Q51, Q52, Q53, Q54, Q55, Q56, Q57, Q58, Q59, Q60, Q61, Q62, Q63, Q64, Q65, Q66, Q67, Q68, Q69, Q70, Q71, Q72, Q73, Q74, Q75, Q76, Q77, Q78, Q79, Q80, Q81, Q82, Q83, Q84, Q85, Q86, Q87, Q88, Q89, Q90, Q91, Q92, Q93, Q94, Q95, Q96, Q97, Q98, Q99, Q100, Q101, Q102, Q103, Q104, Q105, Q106, Q107, Q108, Q109, Q110, Q111, Q112, Q113, Q114, Q115, Q116]), "depth" : 3 * mm, "offsetDistance" : 25 * mm});
        }
    });
